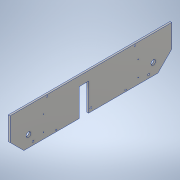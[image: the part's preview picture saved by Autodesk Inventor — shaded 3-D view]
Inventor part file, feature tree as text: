
AUTODESK INVENTOR PART (.ipt)
format: ipt  version: 2021 (Build 250183000, 183)  size: 184,320 bytes
history: native  units: in
note: dims shown in document units (in); Inventor stores cm internally (conversion verified against a paired STEP export)
features: sketch x5, hole x3, extrude x2, chamfer x2, projected_geometry x2
ambient origin geometry x8: Origin, YZ Plane, XZ Plane, XY Plane, X Axis, Y Axis, Z Axis, Center Point
bodies: Solid1 (feature_tree)
feature tree (14):
  extrude  "Extrusion1"  Depth=17.5in
  chamfer  "Chamfer1"  Distance=0.1875in
  chamfer  "Chamfer2"  Distance=1.5in Angle=45.0deg
  hole  "Hole1"  [1 undecoded]
  hole  "Hole2"  [1 undecoded]
  extrude  "Extrusion6"  Depth=3.0in
  hole  "Hole3"  [1 undecoded]
  sketch  "Sketch1"  dims[d0=4.0in d1=17.5in]
  sketch  "Sketch6"  dims[d2=0.501in]
  projected_geometry  "Projected Loop5"
  sketch  "Sketch7"  dims[d3=1.25in]
  projected_geometry  "Projected Loop6"
  sketch  "Sketch8"  dims[d4=2.0in]
  sketch  "Sketch9"  dims[d5=2.0in d6=0.1875in d7=0.0in d8=1.5in d9=0.125in d10=45.0deg d11=1.5in d12=0.125in d13=45.0deg d22=6.517in d23=0.125in d24=0.603in d25=0.125in d26=0.63in d27=6.517in d28=0.125in d29=0.603in d30=6.517in d31=0.125in d32=0.63in d33=6.517in d80=1.7in d83=0.65in d86=1.7in d88=0.08in d89=0.75in d90=0.375in d91=0.25in d92=0.5635in d93=1.0in d94=0.8108in d95=0.175in d96=0.175in d97=0.175in d98=0.175in d99=4.0in d100=4.0in d101=5.0in d102=5.0in d103=0.15in d104=0.75in d105=0.375in d106=0.25in d107=0.5635in d108=1.0in d109=0.8108in d110=1.0in d111=0.0in d112=1.0in d113=7.5in d114=3.0in d115=3.625in d116=3.625in d117=0.65in d118=3.625in d119=3.625in d120=0.375in d121=2.5in d122=2.5in d123=12.5in d124=6.25in d125=0.2in d126=0.75in d127=0.375in d128=0.25in d129=0.5635in d130=0.75in d131=0.8108in]
note: 3 required parameter values undecoded (feature->parameter linkage not recoverable at this tier; creation-order binding heuristic only, values carry confidence <= 0.55)
